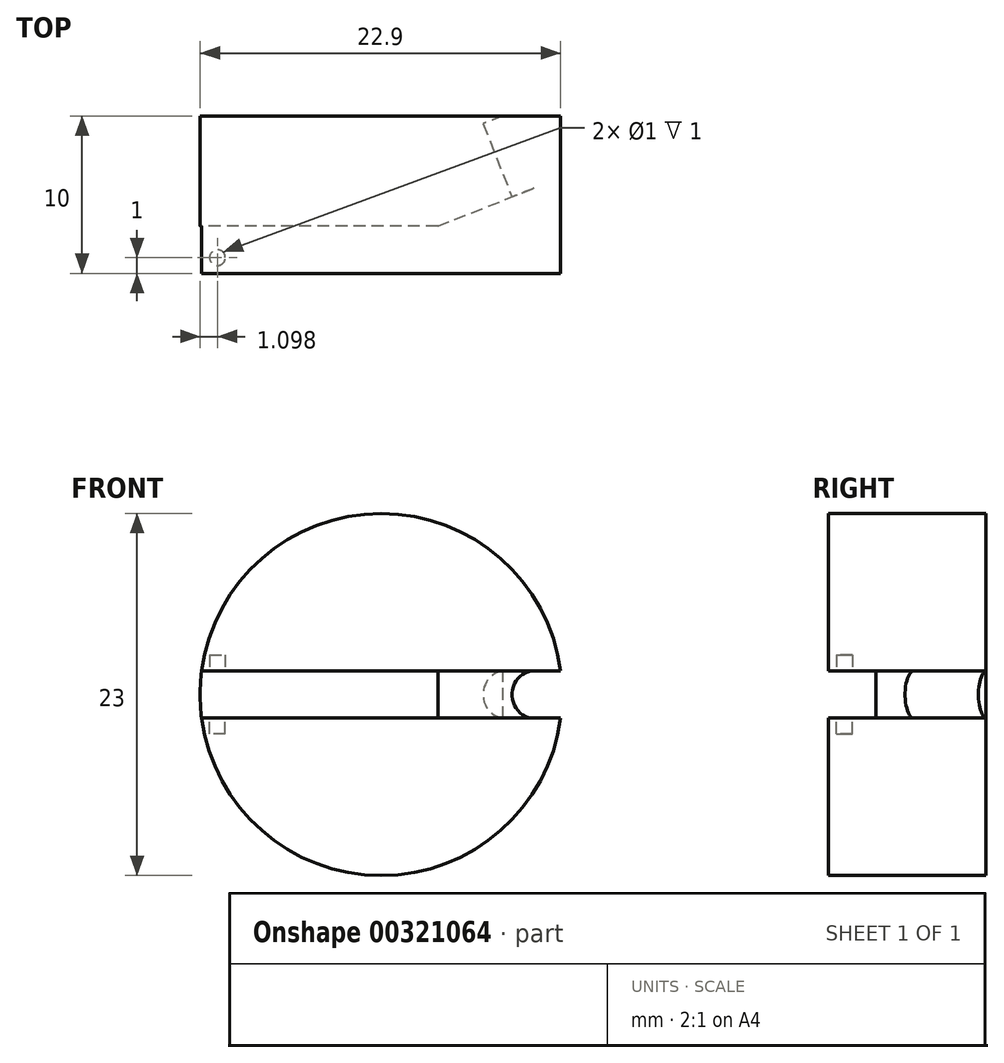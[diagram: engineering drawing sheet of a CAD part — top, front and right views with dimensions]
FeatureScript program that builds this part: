
annotation { "Feature Type Name" : "Feature", "Feature Type Description" : "" }
export const myFeature = defineFeature(function(context is Context, id is Id, definition is map)
    precondition{}
    {
        {
            var Q0;
            Q0=qCreatedBy(makeId("Front.planeOp"),FACE);
            var sketch = newSketch(context, id + "F0", { "sketchPlane" : qUnion([Q0])});
            skCircle(sketch, "E0", {"center": v(0, 0) * mm, "radius": 11.5 * mm});
            skSolve(sketch);
        }
        {
            var Q0;
            Q0 = qSketchRegion(id + "F0", true);
            extrude(context, id + "F1", {"entities" : qUnion([Q0]), "depth" : 10 * mm});
        }
        {
            var Q0;
            Q0=makeQuery(id+"F1.opExtrude","CAP_FACE",FACE,{"disambiguationData":[OSD([sQuery(id+"F0.wireOp",EDGE,"E0")])],"isStart":false});
            var sketch = newSketch(context, id + "F2", { "sketchPlane" : qUnion([Q0])});
            skLineSegment(sketch, "E1.bottom", {"start": v(15, 1.5) * mm, "end": v(-15, 1.5) * mm});
            skLineSegment(sketch, "E1.top", {"start": v(15, -1.5) * mm, "end": v(-15, -1.5) * mm});
            skLineSegment(sketch, "E1.left", {"start": v(15, 1.5) * mm, "end": v(15, -1.5) * mm});
            skLineSegment(sketch, "E1.right", {"start": v(-15, 1.5) * mm, "end": v(-15, -1.5) * mm});
            skPoint(sketch, "E1.middle", {"position": v(0, 0) * mm});
            skSolve(sketch);
        }
        {
            var Q0;
            Q0 = qSketchRegion(id + "F2", true);
            extrude(context, id + "F3", {"entities" : qUnion([Q0]), "operationType" : NewBodyOperationType.REMOVE, "oppositeDirection" : true, "depth" : 3 * mm});
        }
        {
            var Q0;
            Q0=makeQuery(id+"F3.boolean.opBoolean","COPY",FACE,{"derivedFrom":makeQuery(id+"F3.opExtrude","SWEPT_FACE",FACE,{"disambiguationData":[OSD([sQuery(id+"F2.wireOp",EDGE,"E1.bottom")])]})});
            var sketch = newSketch(context, id + "F4", { "sketchPlane" : qUnion([Q0])});
            skCircle(sketch, "E2", {"center": v(-10.4, 9) * mm, "radius": 0.5 * mm});
            skSolve(sketch);
        }
        {
            var Q0;
            Q0 = qSketchRegion(id + "F4", true);
            extrude(context, id + "F5", {"entities" : qUnion([Q0]), "operationType" : NewBodyOperationType.REMOVE, "oppositeDirection" : true, "depth" : 1 * mm});
        }
        {
            var Q0;
            Q0=makeQuery(id+"F3.boolean.opBoolean","COPY",FACE,{"derivedFrom":makeQuery(id+"F3.opExtrude","SWEPT_FACE",FACE,{"disambiguationData":[OSD([sQuery(id+"F2.wireOp",EDGE,"E1.top")])]})});
            var sketch = newSketch(context, id + "F6", { "sketchPlane" : qUnion([Q0])});
            skCircle(sketch, "E3", {"center": v(-10.4, -9) * mm, "radius": 0.5 * mm});
            skSolve(sketch);
        }
        {
            var Q0;
            Q0 = qSketchRegion(id + "F6", true);
            extrude(context, id + "F7", {"entities" : qUnion([Q0]), "operationType" : NewBodyOperationType.REMOVE, "oppositeDirection" : true, "depth" : 1 * mm});
        }
        {
            var Q0;
            Q0=makeQuery(id+"F3.boolean.opBoolean","COPY",FACE,{"derivedFrom":makeQuery(id+"F3.opExtrude","SWEPT_FACE",FACE,{"disambiguationData":[OSD([sQuery(id+"F2.wireOp",EDGE,"E1.top")])]})});
            var sketch = newSketch(context, id + "F8", { "sketchPlane" : qUnion([Q0])});
            skLineSegment(sketch, "E4", {"start": v(3.6, -7) * mm, "end": v(13.95, -2.92) * mm});
            skLineSegment(sketch, "E5", {"start": v(13.95, -2.92) * mm, "end": v(11.4, -7) * mm});
            skLineSegment(sketch, "E6", {"start": v(11.4, -7) * mm, "end": v(3.6, -7) * mm});
            skLineSegment(sketch, "E7", {"start": v(11.4, -7) * mm, "end": v(14.35, -7.3) * mm});
            skLineSegment(sketch, "E8", {"start": v(14.35, -7.3) * mm, "end": v(13.95, -2.92) * mm});
            skSolve(sketch);
        }
        {
            var Q0;
            Q0 = qSketchRegion(id + "F8", true);
            extrude(context, id + "F9", {"entities" : qUnion([Q0]), "operationType" : NewBodyOperationType.REMOVE, "depth" : 3 * mm});
        }
        {
            var Q0;
            Q0=makeQuery(id+"F9.boolean.opBoolean","COPY",FACE,{"derivedFrom":makeQuery(id+"F9.opExtrude","SWEPT_FACE",FACE,{"disambiguationData":[OSD([sQuery(id+"F8.wireOp",EDGE,"E4")])]})});
            var sketch = newSketch(context, id + "F10", { "sketchPlane" : qUnion([Q0])});
            skCircle(sketch, "E9", {"center": v(7.34, 0) * mm, "radius": 1.5 * mm});
            skLineSegment(sketch, "E10", {"start": v(7.34, -1.5) * mm, "end": v(11.19, -1.5) * mm});
            skLineSegment(sketch, "E11", {"start": v(11.19, -1.5) * mm, "end": v(11.19, 1.5) * mm});
            skLineSegment(sketch, "E12", {"start": v(11.19, 1.5) * mm, "end": v(7.34, 1.5) * mm});
            skSolve(sketch);
        }
        {
            var Q0;
            Q0 = qSketchRegion(id + "F10", true);
            extrude(context, id + "F11", {"entities" : qUnion([Q0]), "operationType" : NewBodyOperationType.REMOVE, "oppositeDirection" : true, "depth" : 5 * mm});
        }
    });
